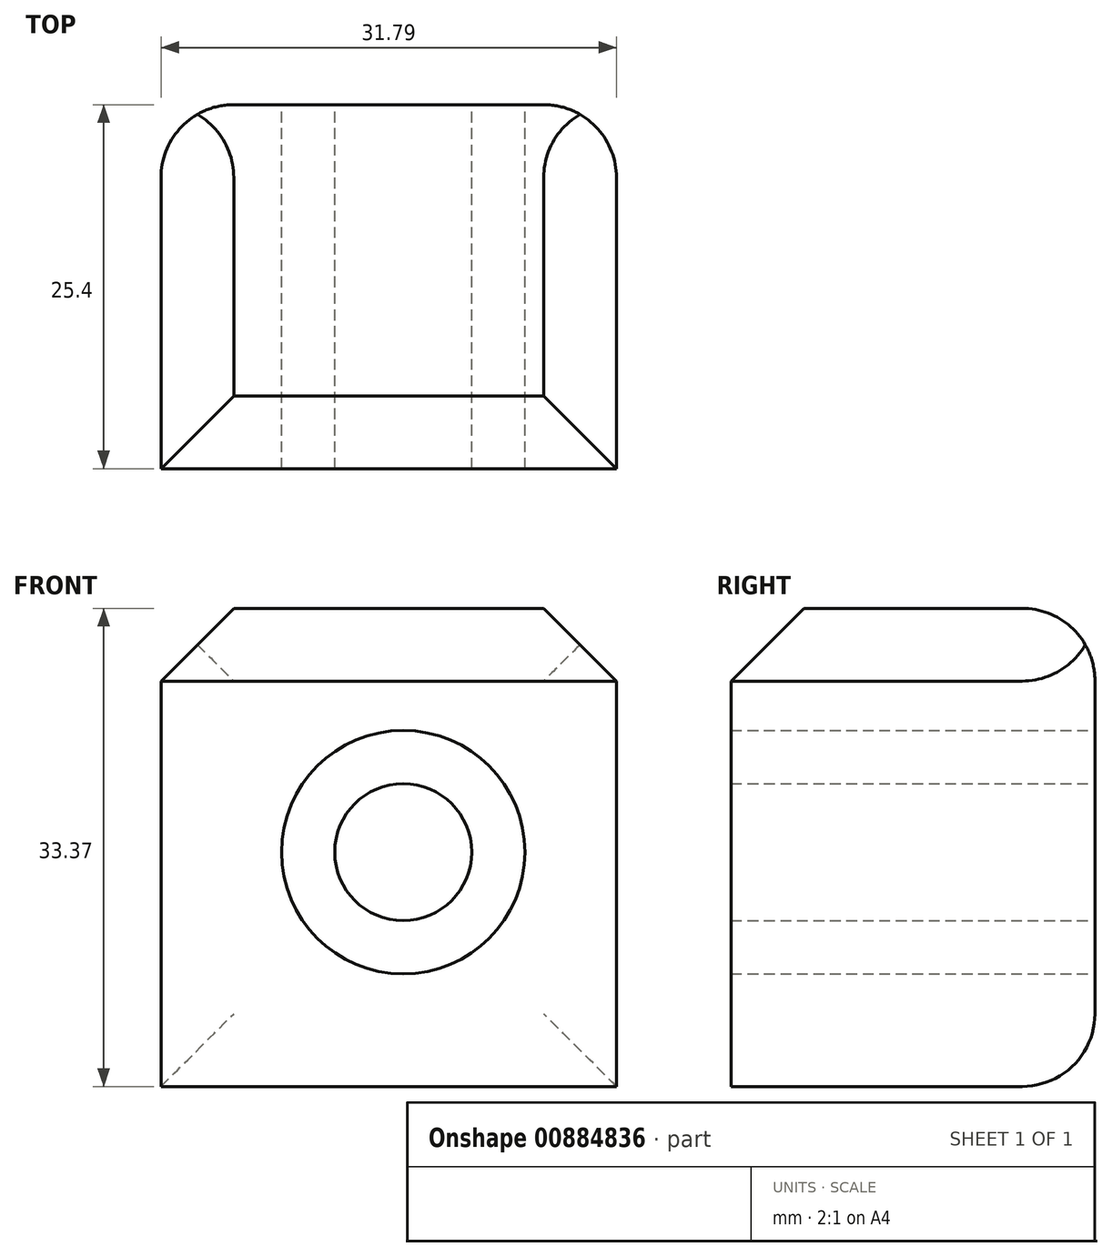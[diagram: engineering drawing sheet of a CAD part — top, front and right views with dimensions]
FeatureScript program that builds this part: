
annotation { "Feature Type Name" : "Feature", "Feature Type Description" : "" }
export const myFeature = defineFeature(function(context is Context, id is Id, definition is map)
    precondition{}
    {
        {
            var Q0;
            Q0=qCreatedBy(makeId("Front.planeOp"),FACE);
            var sketch = newSketch(context, id + "F0", { "sketchPlane" : qUnion([Q0])});
            skLineSegment(sketch, "E0", {"start": v(0, 0) * mm, "end": v(31.79, 0) * mm});
            skLineSegment(sketch, "E1", {"start": v(31.79, 0) * mm, "end": v(31.79, 33.37) * mm});
            skLineSegment(sketch, "E2", {"start": v(31.79, 33.37) * mm, "end": v(0, 33.37) * mm});
            skLineSegment(sketch, "E3", {"start": v(0, 33.37) * mm, "end": v(0, 0) * mm});
            skSolve(sketch);
        }
        {
            var Q0;
            Q0=makeQuery(id+"F0.imprint","IMPRINT",FACE,{"disambiguationData":[TD([[makeQuery(id+"F0.imprint","IMPRINT",EDGE,{"derivedFrom":sQuery(id+"F0.wireOp",EDGE,"E0")}),1.0]])]});
            extrude(context, id + "F1", {"entities" : qUnion([Q0]), "depth" : 25.4 * mm, "offsetDistance" : 25.4 * mm});
        }
        {
            var Q0;
            Q0=makeQuery(id+"F1.opExtrude","CAP_FACE",FACE,{"disambiguationData":[OSD([sQuery(id+"F0.wireOp",EDGE,"E0"),sQuery(id+"F0.wireOp",EDGE,"E1"),sQuery(id+"F0.wireOp",EDGE,"E2"),sQuery(id+"F0.wireOp",EDGE,"E3")])],"isStart":true});
            var sketch = newSketch(context, id + "F2", { "sketchPlane" : qUnion([Q0])});
            skCircle(sketch, "E4", {"center": v(-16.9, 16.35) * mm, "radius": 8.5 * mm});
            skCircle(sketch, "E5", {"center": v(-16.9, 16.35) * mm, "radius": 4.78 * mm});
            skSolve(sketch);
        }
        {
            var Q0;
            Q0=makeQuery(id+"F2.imprint","IMPRINT",FACE,{"disambiguationData":[TD([[makeQuery(id+"F2.imprint","IMPRINT",EDGE,{"derivedFrom":sQuery(id+"F2.wireOp",EDGE,"E4")}),1.0]])]});
            extrude(context, id + "F3", {"entities" : qUnion([Q0]), "operationType" : NewBodyOperationType.REMOVE, "endBound" : BoundingType.THROUGH_ALL, "oppositeDirection" : true, "depth" : 25.4 * mm, "offsetDistance" : 25.4 * mm});
        }
        {
            var Q0;
            Q0=makeQuery(id+"F1.opExtrude","CAP_EDGE",EDGE,{"disambiguationData":[OSD([sQuery(id+"F0.wireOp",EDGE,"E2")])],"isStart":true});
            var Q1;
            Q1=makeQuery(id+"F1.opExtrude","CAP_EDGE",EDGE,{"disambiguationData":[OSD([sQuery(id+"F0.wireOp",EDGE,"E3")])],"isStart":true});
            var Q2;
            Q2=makeQuery(id+"F1.opExtrude","CAP_EDGE",EDGE,{"disambiguationData":[OSD([sQuery(id+"F0.wireOp",EDGE,"E0")])],"isStart":true});
            var Q3;
            Q3=makeQuery(id+"F1.opExtrude","CAP_EDGE",EDGE,{"disambiguationData":[OSD([sQuery(id+"F0.wireOp",EDGE,"E1")])],"isStart":true});
            fillet(context, id + "F4", {"entities" : qUnion([Q0, Q1, Q2, Q3]), "radius" : 5.08 * mm, "tangentPropagation" : true, "allowEdgeOverflow" : false});
        }
        {
            var Q0;
            Q0=makeQuery(id+"F1.opExtrude","CAP_EDGE",EDGE,{"disambiguationData":[OSD([sQuery(id+"F0.wireOp",EDGE,"E2")])],"isStart":false});
            var Q1;
            Q1=makeQuery(id+"F1.opExtrude","SWEPT_EDGE",EDGE,{"disambiguationData":[OSD([sQuery(id+"F0.wireOp",EDGE,"E1"),sQuery(id+"F0.wireOp",EDGE,"E2")])]});
            var Q2;
            Q2=makeQuery(id+"F1.opExtrude","SWEPT_EDGE",EDGE,{"disambiguationData":[OSD([sQuery(id+"F0.wireOp",EDGE,"E2"),sQuery(id+"F0.wireOp",EDGE,"E3")])]});
            var Q3;
            {var subQ0=sQuery(id+"F0.wireOp",EDGE,"E2");Q3=makeQuery(id+"F4.opFillet","BLEND_EDGE",EDGE,{"blendedFrom":[makeQuery(id+"F1.opExtrude","CAP_EDGE",EDGE,{"disambiguationData":[OSD([subQ0])],"isStart":true}),makeQuery(id+"F1.opExtrude","SWEPT_FACE",FACE,{"disambiguationData":[OSD([subQ0])]})],"blendedInto":[makeQuery(id+"F1.opExtrude","SWEPT_FACE",FACE,{"disambiguationData":[OSD([subQ0])]})]});}
            chamfer(context, id + "F5", {"entities" : qUnion([Q0, Q1, Q2, Q3]), "width" : 5.08 * mm, "tangentPropagation" : true});
        }
    });
